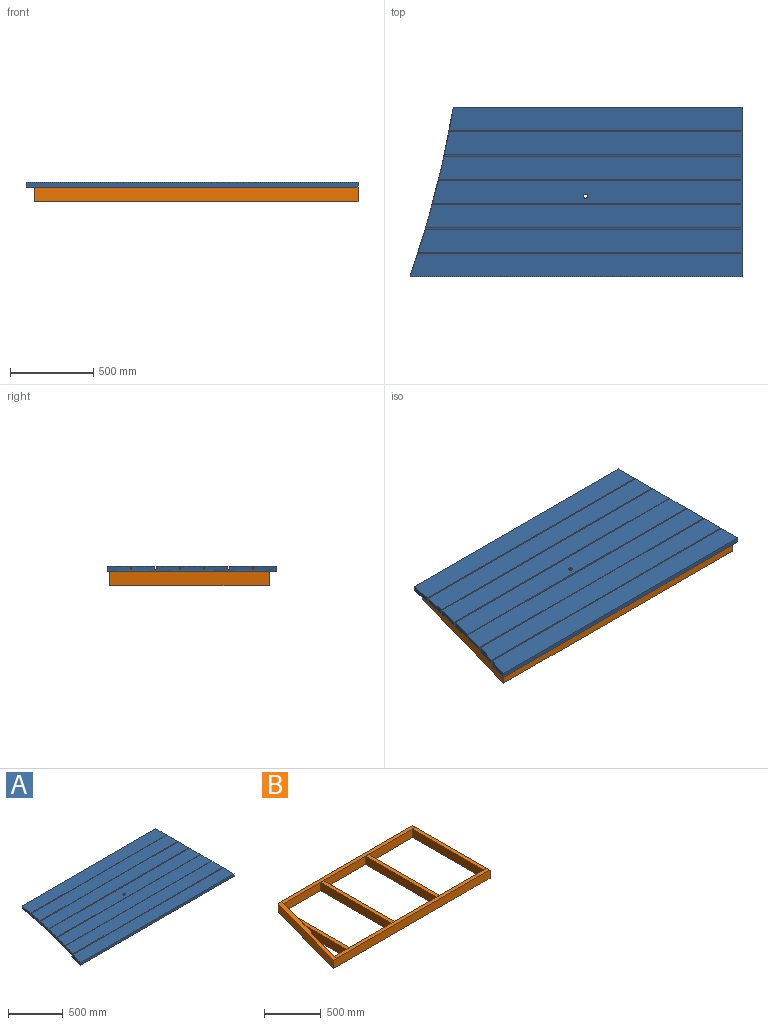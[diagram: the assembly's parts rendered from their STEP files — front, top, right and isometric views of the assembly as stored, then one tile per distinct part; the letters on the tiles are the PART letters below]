
ASSEMBLY  parts=2 mates=1
PART A: 31 faces, bbox 1993.6x1016x29.4 mm
  f0: cylinder r=6096mm len=1016mm, axis (0,0,-1), area 29965.1mm2, adj f1,f2,f3,f4,f5,f6,f7,f9
  f1: plane 1787.89x139.7mm, normal (0,0,1), area 247744.2mm2, adj f0,f8,f25,f28
  f2: plane 1821.26x139.7mm, normal (0,0,1), area 252154.7mm2, adj f0,f8,f22,f24
  f3: plane 1858.44x139.7mm, normal (0,0,1), area 256586.4mm2, adj f0,f8,f19,f21,f30
  f4: plane 1899.5x139.7mm, normal (0,0,1), area 262568.9mm2, adj f0,f8,f16,f18
  f5: plane 1944.52x139.7mm, normal (0,0,1), area 268593.1mm2, adj f0,f8,f13,f15
  f6: plane 1993.61x139.7mm, normal (0,0,1), area 275177.9mm2, adj f0,f7,f8,f12
  f7: plane 1993.61x29.37mm, normal (0,-1,0), area 58549.8mm2, adj f0,f6,f8,f11
  f8: plane 1016x29.37mm, normal (1,0,0), area 28991.9mm2, adj f1,f2,f3,f4,f5,f6,f7,f9
  f9: plane 1733.39x29.37mm, normal (0,1,0), area 50907.5mm2, adj f0,f8,f10,f11
  f10: plane 1758.27x139.7mm, normal (0,0,1), area 243853.4mm2, adj f0,f8,f9,f27
  f11: plane 1993.61x1016mm, normal (0,0,-1), area 1877003.3mm2, adj f0,f7,f8,f9,f30
  f12: plane 1946.57x22.23mm, normal (0,1,0), area 43262.6mm2, adj f0,f6,f8,f14
  f13: plane 1944.52x22.23mm, normal (0,-1,0), area 43217mm2, adj f0,f5,f8,f14
  f14: plane 1946.57x6.35mm, normal (0,0,1), area 12354.2mm2, adj f0,f8,f12,f13
  f15: plane 1901.37x22.23mm, normal (0,1,0), area 42258mm2, adj f0,f5,f8,f17
  f16: plane 1899.5x22.23mm, normal (0,-1,0), area 42216.3mm2, adj f0,f4,f8,f17
  f17: plane 1901.37x6.35mm, normal (0,0,1), area 12067.8mm2, adj f0,f8,f15,f16
  f18: plane 1860.14x22.23mm, normal (0,1,0), area 41341.6mm2, adj f0,f4,f8,f20
  f19: plane 1858.44x22.23mm, normal (0,-1,0), area 41303.8mm2, adj f0,f3,f8,f20
  f20: plane 1860.14x6.35mm, normal (0,0,1), area 11806.5mm2, adj f0,f8,f18,f19
  f21: plane 1822.8x22.23mm, normal (0,1,0), area 40511.6mm2, adj f0,f3,f8,f23
  f22: plane 1821.26x22.23mm, normal (0,-1,0), area 40477.5mm2, adj f0,f2,f8,f23
  f23: plane 1822.8x6.35mm, normal (0,0,1), area 11569.9mm2, adj f0,f8,f21,f22
  f24: plane 1789.26x22.23mm, normal (0,1,0), area 39766.4mm2, adj f0,f2,f8,f26
  f25: plane 1787.89x22.23mm, normal (0,-1,0), area 39735.9mm2, adj f0,f1,f8,f26
  f26: plane 1789.26x6.35mm, normal (0,0,1), area 11357.5mm2, adj f0,f8,f24,f25
  f27: plane 1758.27x22.23mm, normal (0,-1,0), area 39077.5mm2, adj f0,f8,f10,f29
  f28: plane 1759.48x22.23mm, normal (0,1,0), area 39104.4mm2, adj f0,f1,f8,f29
  f29: plane 1759.48x6.35mm, normal (0,0,1), area 11168.9mm2, adj f0,f8,f27,f28
  f30: cylinder r=12.7mm len=29.37mm, axis (0,0,1), area 2343.5mm2, adj f3,f11
PART B: 42 faces, bbox 1943.1x958.9x88.9 mm
  f0: plane 1676.05x88.9mm, normal (0,1,0), area 149000.6mm2, adj f8,f9,f15,f17,f20,f21,f38,f39
  f1: plane 1892.94x88.9mm, normal (0,1,0), area 155120.9mm2, adj f3,f4,f5,f6,f7,f8,f10,f17
  f2: plane 1647.11x88.9mm, normal (0,-1,0), area 136557mm2, adj f3,f4,f5,f6,f7,f8,f17,f20
  f3: plane 882.65x88.9mm, normal (-1,0,0), area 78467.5mm2, adj f1,f2,f13,f21,f34,f35,f36,f37
  f4: plane 882.65x88.9mm, normal (1,0,0), area 78467.5mm2, adj f1,f2,f13,f21,f34,f35,f36,f37
  f5: plane 882.65x88.9mm, normal (-1,0,0), area 78467.5mm2, adj f1,f2,f12,f21,f30,f31,f32,f33
  f6: plane 882.65x88.9mm, normal (1,0,0), area 78467.5mm2, adj f1,f2,f12,f21,f30,f31,f32,f33
  f7: plane 882.65x88.9mm, normal (-1,0,0), area 78467.5mm2, adj f1,f2,f11,f21,f22,f23,f24,f25
  f8: plane 958.85x88.9mm, normal (1,0,0), area 85241.6mm2, adj f0,f1,f2,f10,f11,f16,f20,f21
  f9: plane 958.85x306.6mm, normal (0,0,1), area 37922.6mm2, adj f0,f15,f16,f17
  f10: plane 1903.52x38.1mm, normal (0,0,1), area 72322.1mm2, adj f1,f8,f16,f40
  f11: plane 882.6x38.1mm, normal (0,0,1), area 33627.1mm2, adj f7,f8,f23,f25
  f12: plane 882.6x38.1mm, normal (0,0,1), area 33627.1mm2, adj f5,f6,f31,f33
  f13: plane 882.6x38.1mm, normal (0,0,1), area 33627.1mm2, adj f3,f4,f35,f37
  f14: plane 661.07x38.1mm, normal (0,0,1), area 22580.7mm2, adj f18,f19,f27,f29
  f15: plane 958.85x267.05mm, normal (-0.96,0.27,0), area 88486.1mm2, adj f0,f9,f16,f21
  f16: plane 1943.1x88.9mm, normal (0,-1,0), area 172741.5mm2, adj f8,f9,f10,f15,f17,f21,f40,f41
  f17: plane 958.85x267.05mm, normal (0.96,-0.27,0), area 69391.5mm2, adj f0,f1,f2,f9,f16,f18,f19,f21
  f18: plane 524.39x88.9mm, normal (-1,0,0), area 46618mm2, adj f1,f14,f17,f21,f26,f27,f28,f29
  f19: plane 661.19x88.9mm, normal (1,0,0), area 58779.3mm2, adj f1,f14,f17,f21,f26,f27,f28,f29
  f20: plane 1647.08x38.1mm, normal (0,0,1), area 62551.7mm2, adj f0,f2,f8,f39
  f21: plane 1943.1x958.85mm, normal (0,0,-1), area 296270.6mm2, adj f0,f1,f2,f3,f4,f5,f6,f7
  f22: plane 38.1x0.03mm, normal (0,0,1), area 1mm2, adj f1,f7,f8,f23
  f23: plane 38.1x2.54mm, normal (0,-1,0), area 96.8mm2, adj f7,f8,f11,f22
  f24: plane 38.1x0.02mm, normal (0,0,1), area 0.9mm2, adj f2,f7,f8,f25
  f25: plane 38.1x2.54mm, normal (0,1,0), area 96.8mm2, adj f7,f8,f11,f24
  f26: plane 38.1x0.03mm, normal (0,0,1), area 1mm2, adj f1,f18,f19,f27
  f27: plane 38.1x2.54mm, normal (0,-1,0), area 96.8mm2, adj f14,f18,f19,f26
  f28: plane 136.89x38.1mm, normal (0,0,1), area 3.6mm2, adj f17,f18,f19,f29
  f29: plane 136.8x38.1mm, normal (-0.96,0.27,0), area 360.7mm2, adj f14,f18,f19,f28
  f30: plane 38.1x0.03mm, normal (0,0,1), area 1mm2, adj f1,f5,f6,f31
  f31: plane 38.1x2.54mm, normal (0,-1,0), area 96.8mm2, adj f5,f6,f12,f30
  f32: plane 38.1x0.02mm, normal (0,0,1), area 0.9mm2, adj f2,f5,f6,f33
  f33: plane 38.1x2.54mm, normal (0,1,0), area 96.8mm2, adj f5,f6,f12,f32
  f34: plane 38.1x0.03mm, normal (0,0,1), area 1mm2, adj f1,f3,f4,f35
  f35: plane 38.1x2.54mm, normal (0,-1,0), area 96.8mm2, adj f3,f4,f13,f34
  f36: plane 38.1x0.02mm, normal (0,0,1), area 0.9mm2, adj f2,f3,f4,f37
  f37: plane 38.1x2.54mm, normal (0,1,0), area 96.8mm2, adj f3,f4,f13,f36
  f38: plane 38.1x10.64mm, normal (0,0,1), area 1mm2, adj f0,f2,f17,f39
  f39: plane 38.1x10.61mm, normal (-0.96,0.27,0), area 100.5mm2, adj f0,f2,f20,f38
  f40: plane 38.1x10.61mm, normal (-0.96,0.27,0), area 100.5mm2, adj f1,f10,f16,f41
  f41: plane 38.1x10.64mm, normal (0,0,1), area 1mm2, adj f1,f16,f17,f40
PLACE A t=(-523.24,-684.61,88.9)mm
PLACE B t=(-523.24,-678.26,0)mm
MATE fastened B.f20 <-> A.f11  axis (0,0,1) through (0,479.42,88.9)mm
